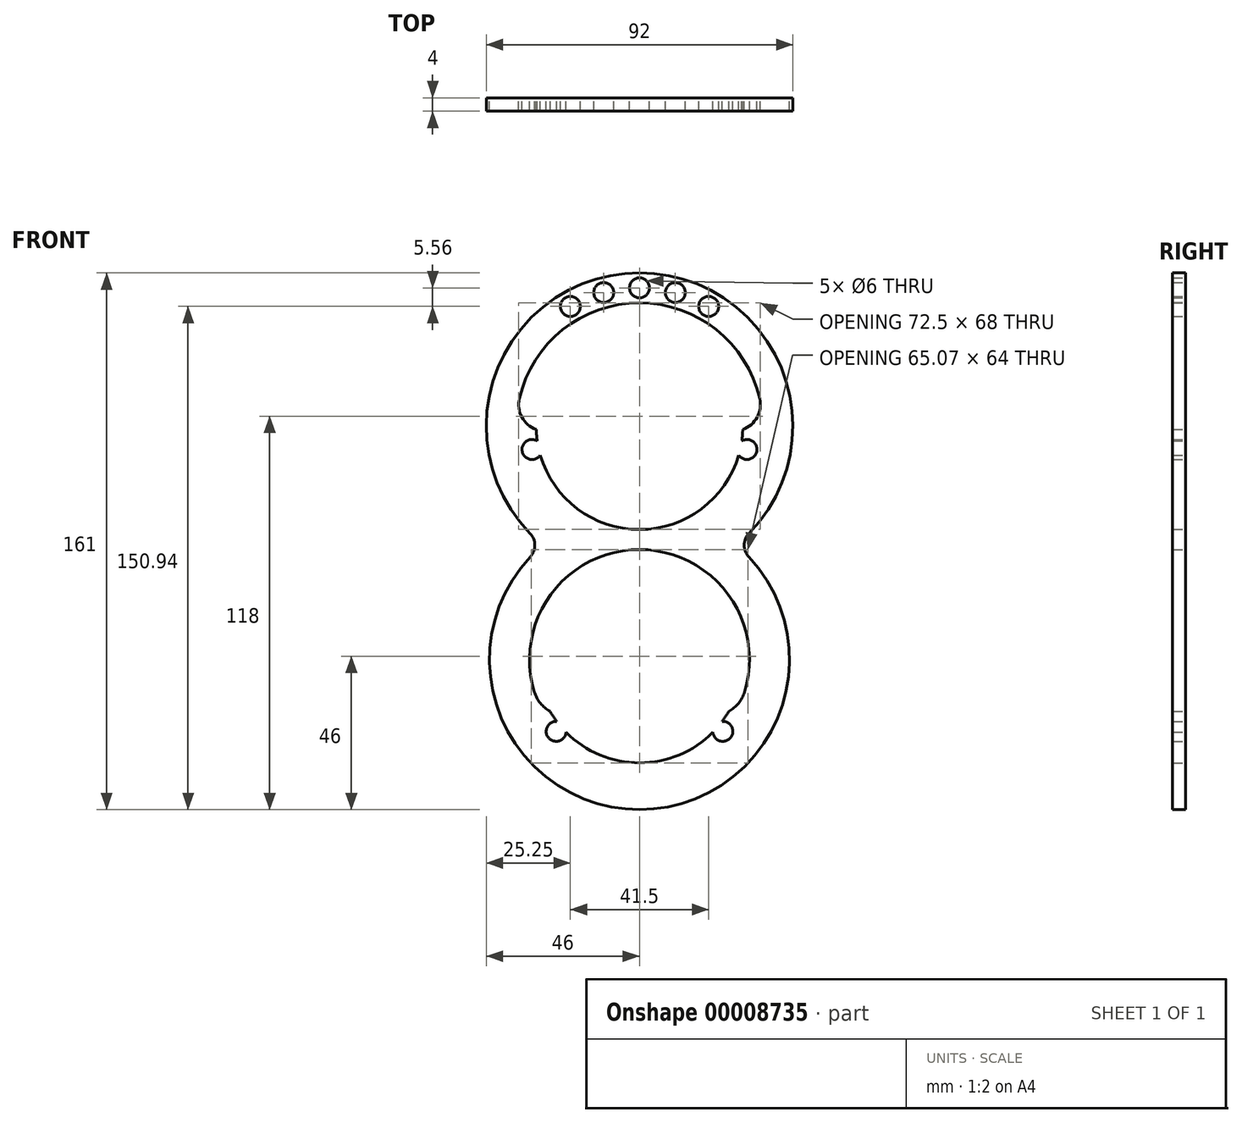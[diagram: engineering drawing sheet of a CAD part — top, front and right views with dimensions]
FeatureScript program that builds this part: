
annotation { "Feature Type Name" : "Feature", "Feature Type Description" : "" }
export const myFeature = defineFeature(function(context is Context, id is Id, definition is map)
    precondition{}
    {
        {
            var Q0;
            Q0=qCreatedBy(makeId("Front.planeOp"),FACE);
            var sketch = newSketch(context, id + "F0", { "sketchPlane" : qUnion([Q0])});
            skCircle(sketch, "E0", {"center": v(0, 0) * mm, "radius": 30 * mm, "construction": true});
            skArc(sketch, "E1", {"start": v(-30.68, -4.44) * mm, "mid": v(-35.18, -7.63) * mm, "end": v(-29.76, -8.67) * mm});
            skArc(sketch, "E2", {"start": v(32.83, -32.22) * mm, "mid": v(0, 46) * mm, "end": v(-32.83, -32.22) * mm});
            skArc(sketch, "E3", {"start": v(-29.76, -8.67) * mm, "mid": v(0, -31) * mm, "end": v(29.76, -8.67) * mm});
            skArc(sketch, "E4.trimOffspring", {"start": v(30.68, -4.44) * mm, "mid": v(30.88, -2.72) * mm, "end": v(30.98, -1) * mm});
            skArc(sketch, "E5.trimOffspring", {"start": v(29.76, -8.67) * mm, "mid": v(35.18, -7.63) * mm, "end": v(30.68, -4.44) * mm});
            skArc(sketch, "E6.trimOffspring", {"start": v(36.05, 8.33) * mm, "mid": v(0, 37) * mm, "end": v(-36.05, 8.33) * mm});
            skArc(sketch, "E7", {"start": v(-36.05, 8.33) * mm, "mid": v(-35.28, 2.7) * mm, "end": v(-30.98, -1) * mm});
            skLineSegment(sketch, "E8", {"start": v(0, -7) * mm, "end": v(0, 0) * mm, "construction": true});
            skArc(sketch, "E9.0.MirrorCS", {"start": v(36.05, 8.33) * mm, "mid": v(35.28, 2.7) * mm, "end": v(30.98, -1) * mm});
            skArc(sketch, "E10.trimOffspring", {"start": v(-30.98, -1) * mm, "mid": v(-30.88, -2.72) * mm, "end": v(-30.68, -4.44) * mm});
            skLineSegment(sketch, "E11", {"start": v(0, 37) * mm, "end": v(0, 46) * mm, "construction": true});
            skCircle(sketch, "E12", {"center": v(0, 41.5) * mm, "radius": 3 * mm});
            skCircle(sketch, "E13.1.0", {"center": v(10.74, 40.09) * mm, "radius": 3 * mm});
            skCircle(sketch, "E13.2.0", {"center": v(20.75, 35.94) * mm, "radius": 3 * mm});
            skLineSegment(sketch, "E13.anchor1", {"start": v(0, 0) * mm, "end": v(0, 41.5) * mm, "construction": true});
            skLineSegment(sketch, "E13.anchor2", {"start": v(0, 0) * mm, "end": v(20.75, 35.94) * mm, "construction": true});
            skCircle(sketch, "E14.1.0", {"center": v(-10.74, 40.09) * mm, "radius": 3 * mm});
            skCircle(sketch, "E14.2.0", {"center": v(-20.75, 35.94) * mm, "radius": 3 * mm});
            skLineSegment(sketch, "E14.anchor2", {"start": v(0, 0) * mm, "end": v(-20.75, 35.94) * mm, "construction": true});
            skLineSegment(sketch, "E15", {"start": v(-30.98, -1) * mm, "end": v(30.98, -1) * mm, "construction": true});
            skLineSegment(sketch, "E16", {"start": v(-32.25, -7) * mm, "end": v(32.25, -7) * mm, "construction": true});
            skCircle(sketch, "E17", {"center": v(0, -70) * mm, "radius": 30 * mm, "construction": true});
            skArc(sketch, "E18", {"start": v(-22.01, -91.83) * mm, "mid": v(0, -101) * mm, "end": v(22.01, -91.83) * mm});
            skArc(sketch, "E19", {"start": v(-32.76, -39.15) * mm, "mid": v(0, -115) * mm, "end": v(32.76, -39.15) * mm});
            skLineSegment(sketch, "E20", {"start": v(0, -70) * mm, "end": v(0, -39) * mm, "construction": true});
            skLineSegment(sketch, "E21", {"start": v(0, -70) * mm, "end": v(45, -70) * mm, "construction": true});
            skArc(sketch, "E22", {"start": v(-24.84, -88.54) * mm, "mid": v(-27.18, -93.6) * mm, "end": v(-22, -91.54) * mm});
            skArc(sketch, "E23", {"start": v(22, -91.54) * mm, "mid": v(27.18, -93.6) * mm, "end": v(24.84, -88.54) * mm});
            skLineSegment(sketch, "E24", {"start": v(-25, -91.54) * mm, "end": v(25, -91.54) * mm, "construction": true});
            skArc(sketch, "E25", {"start": v(31.53, -79.75) * mm, "mid": v(0, -37) * mm, "end": v(-31.53, -79.75) * mm});
            skArc(sketch, "E26", {"start": v(-31.53, -79.75) * mm, "mid": v(-29.74, -83.1) * mm, "end": v(-26.82, -85.54) * mm});
            skArc(sketch, "E27.0.MirrorCS", {"start": v(31.53, -79.75) * mm, "mid": v(29.74, -83.1) * mm, "end": v(26.82, -85.54) * mm});
            skArc(sketch, "E28.trimOffspring", {"start": v(24.84, -88.54) * mm, "mid": v(25.88, -87.07) * mm, "end": v(26.82, -85.54) * mm});
            skArc(sketch, "E29.trimOffspring", {"start": v(-26.82, -85.54) * mm, "mid": v(-25.88, -87.07) * mm, "end": v(-24.84, -88.54) * mm});
            skLineSegment(sketch, "E30", {"start": v(-26.82, -85.54) * mm, "end": v(26.82, -85.54) * mm, "construction": true});
            skPoint(sketch, "E31.visualSharp", {"position": v(-29.07, -35.65) * mm});
            skArc(sketch, "E31.filletArc", {"start": v(-32.76, -39.15) * mm, "mid": v(-31.4, -35.67) * mm, "end": v(-32.83, -32.22) * mm});
            skPoint(sketch, "E32.visualSharp", {"position": v(29.07, -35.65) * mm});
            skArc(sketch, "E32.filletArc", {"start": v(32.83, -32.22) * mm, "mid": v(31.4, -35.67) * mm, "end": v(32.76, -39.15) * mm});
            skSolve(sketch);
        }
        {
            var Q0;
            Q0 = qSketchRegion(id + "F0", true);
            extrude(context, id + "F1", {"entities" : qUnion([Q0]), "depth" : 4 * mm});
        }
    });
